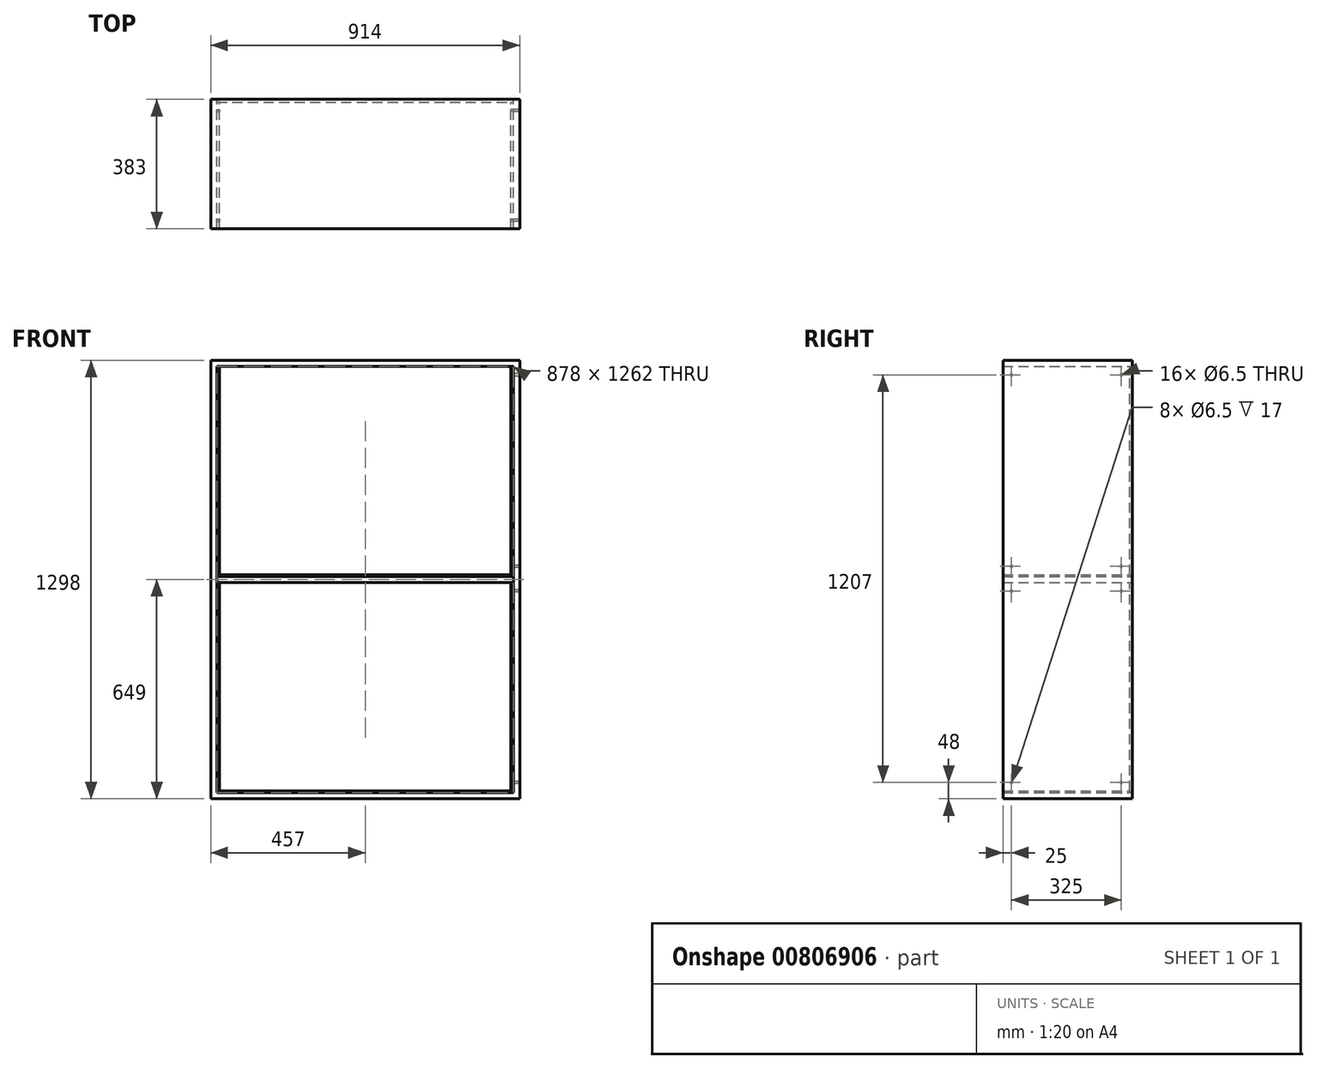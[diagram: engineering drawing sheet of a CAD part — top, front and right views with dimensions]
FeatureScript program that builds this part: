
annotation { "Feature Type Name" : "Feature", "Feature Type Description" : "" }
export const myFeature = defineFeature(function(context is Context, id is Id, definition is map)
    precondition{}
    {
        {
            var Q0;
            Q0=qCreatedBy(makeId("Front.planeOp"),FACE);
            var sketch = newSketch(context, id + "F0", { "sketchPlane" : qUnion([Q0])});
            skLineSegment(sketch, "E0.bottom", {"start": v(457, -649) * mm, "end": v(-457, -649) * mm});
            skLineSegment(sketch, "E0.top", {"start": v(457, 649) * mm, "end": v(-457, 649) * mm});
            skLineSegment(sketch, "E0.left", {"start": v(457, -649) * mm, "end": v(457, 649) * mm});
            skLineSegment(sketch, "E0.right", {"start": v(-457, -649) * mm, "end": v(-457, 649) * mm});
            skPoint(sketch, "E0.middle", {"position": v(0, 0) * mm});
            skLineSegment(sketch, "E1.bottom", {"start": v(439, 631) * mm, "end": v(-439, 631) * mm});
            skLineSegment(sketch, "E1.top", {"start": v(439, -631) * mm, "end": v(-439, -631) * mm});
            skLineSegment(sketch, "E1.left", {"start": v(439, 631) * mm, "end": v(439, -631) * mm});
            skLineSegment(sketch, "E1.right", {"start": v(-439, 631) * mm, "end": v(-439, -631) * mm});
            skLineSegment(sketch, "E2", {"start": v(-439, 0) * mm, "end": v(-457, 0) * mm, "construction": true});
            skLineSegment(sketch, "E3", {"start": v(439, 0) * mm, "end": v(457, 0) * mm, "construction": true});
            skLineSegment(sketch, "E4", {"start": v(0, 631) * mm, "end": v(0, 649) * mm, "construction": true});
            skLineSegment(sketch, "E5", {"start": v(0, -631) * mm, "end": v(0, -649) * mm, "construction": true});
            skSolve(sketch);
        }
        {
            var Q0;
            Q0 = qSketchRegion(id + "F0", true);
            extrude(context, id + "F1", {"entities" : qUnion([Q0]), "depth" : (375 + 8) * mm, "offsetDistance" : 25 * mm});
        }
        {
            var Q0;
            Q0=makeQuery(id+"F1.opExtrude","SWEPT_FACE",FACE,{"disambiguationData":[OSD([sQuery(id+"F0.wireOp",EDGE,"E1.right")])]});
            var sketch = newSketch(context, id + "F2", { "sketchPlane" : qUnion([Q0])});
            skLineSegment(sketch, "E6.bottom", {"start": v(-383, 9) * mm, "end": v(0, 9) * mm});
            skLineSegment(sketch, "E6.top", {"start": v(-383, -9) * mm, "end": v(0, -9) * mm});
            skLineSegment(sketch, "E6.left", {"start": v(-383, 9) * mm, "end": v(-383, -9) * mm});
            skLineSegment(sketch, "E6.right", {"start": v(0, 9) * mm, "end": v(0, -9) * mm});
            skSolve(sketch);
        }
        {
            var Q0;
            Q0 = qSketchRegion(id + "F2", true);
            var Q1;
            Q1=makeQuery(id+"F1.opExtrude","SWEPT_FACE",FACE,{"disambiguationData":[OSD([sQuery(id+"F0.wireOp",EDGE,"E1.left")])]});
            extrude(context, id + "F3", {"entities" : qUnion([Q0]), "endBound" : BoundingType.UP_TO_SURFACE, "depth" : 25 * mm, "endBoundEntityFace" : qUnion([Q1]), "offsetDistance" : 25 * mm});
        }
        {
            var Q0;
            Q0=makeQuery(id+"F3.opExtrude","SWEPT_FACE",FACE,{"disambiguationData":[OSD([sQuery(id+"F2.wireOp",EDGE,"E6.bottom")])]});
            var sketch = newSketch(context, id + "F4", { "sketchPlane" : qUnion([Q0])});
            skLineSegment(sketch, "E7.bottom", {"start": v(-439, -383) * mm, "end": v(439, -383) * mm});
            skLineSegment(sketch, "E7.top", {"start": v(-439, -8) * mm, "end": v(439, -8) * mm});
            skLineSegment(sketch, "E7.left", {"start": v(-439, -383) * mm, "end": v(-439, -8) * mm});
            skLineSegment(sketch, "E7.right", {"start": v(439, -383) * mm, "end": v(439, -8) * mm});
            skSolve(sketch);
        }
        {
            var Q0;
            Q0 = qSketchRegion(id + "F4", true);
            extrude(context, id + "F5", {"entities" : qUnion([Q0]), "depth" : 5 * mm, "offsetDistance" : 25 * mm});
        }
        {
            var Q0;
            Q0=makeQuery(id+"F1.opExtrude","SWEPT_FACE",FACE,{"disambiguationData":[OSD([sQuery(id+"F0.wireOp",EDGE,"E1.left")])]});
            var sketch = newSketch(context, id + "F6", { "sketchPlane" : qUnion([Q0])});
            skLineSegment(sketch, "E8.bottom", {"start": v(383, 14) * mm, "end": v(8, 14) * mm});
            skLineSegment(sketch, "E8.top", {"start": v(383, 631) * mm, "end": v(8, 631) * mm});
            skLineSegment(sketch, "E8.left", {"start": v(383, 14) * mm, "end": v(383, 631) * mm});
            skLineSegment(sketch, "E8.right", {"start": v(8, 14) * mm, "end": v(8, 631) * mm});
            skSolve(sketch);
        }
        {
            var Q0;
            Q0 = qSketchRegion(id + "F6", true);
            extrude(context, id + "F7", {"entities" : qUnion([Q0]), "depth" : 8 * mm, "offsetDistance" : 25 * mm});
        }
        {
            var Q0;
            Q0=makeQuery(id+"F7.opExtrude","CAP_FACE",FACE,{"disambiguationData":[OSD([sQuery(id+"F6.wireOp",EDGE,"E8.bottom"),sQuery(id+"F6.wireOp",EDGE,"E8.top"),sQuery(id+"F6.wireOp",EDGE,"E8.left"),sQuery(id+"F6.wireOp",EDGE,"E8.right")])],"isStart":false});
            var sketch = newSketch(context, id + "F8", { "sketchPlane" : qUnion([Q0])});
            skCircle(sketch, "E9", {"center": v(358, 39) * mm, "radius": 3.25 * mm});
            skLineSegment(sketch, "E10", {"start": v(358, 39) * mm, "end": v(383, 39) * mm, "construction": true});
            skLineSegment(sketch, "E11", {"start": v(358, 39) * mm, "end": v(358, 14) * mm, "construction": true});
            skCircle(sketch, "E12.0.1.0", {"center": v(358, 606) * mm, "radius": 3.25 * mm});
            skCircle(sketch, "E12.1.0.0", {"center": v(33, 39) * mm, "radius": 3.25 * mm});
            skCircle(sketch, "E12.1.1.0", {"center": v(33, 606) * mm, "radius": 3.25 * mm});
            skLineSegment(sketch, "E12.direction1", {"start": v(358, 39) * mm, "end": v(33, 39) * mm, "construction": true});
            skLineSegment(sketch, "E12.direction2", {"start": v(358, 39) * mm, "end": v(358, 606) * mm, "construction": true});
            skSolve(sketch);
        }
        {
            var Q0;
            Q0 = qSketchRegion(id + "F8", true);
            extrude(context, id + "F9", {"entities" : qUnion([Q0]), "operationType" : NewBodyOperationType.REMOVE, "oppositeDirection" : true, "depth" : 25 * mm, "offsetDistance" : 25 * mm});
        }
        {
            var Q0;
            Q0=makeQuery(id+"F7.opExtrude","SWEPT_BODY",BODY,{"disambiguationData":[OSD([sQuery(id+"F6.wireOp",EDGE,"E8.bottom"),sQuery(id+"F6.wireOp",EDGE,"E8.top"),sQuery(id+"F6.wireOp",EDGE,"E8.left"),sQuery(id+"F6.wireOp",EDGE,"E8.right")])]});
            var Q1;
            Q1=qCreatedBy(makeId("Right.planeOp"),FACE);
            mirror(context, id + "F10", {"entities" : qUnion([Q0]), "mirrorPlane" : qUnion([Q1])});
        }
        {
            var Q0;
            Q0=makeQuery(id+"F5.opExtrude","SWEPT_BODY",BODY,{"disambiguationData":[OSD([sQuery(id+"F4.wireOp",EDGE,"E7.bottom"),sQuery(id+"F4.wireOp",EDGE,"E7.top"),sQuery(id+"F4.wireOp",EDGE,"E7.left"),sQuery(id+"F4.wireOp",EDGE,"E7.right")])]});
            transform(context, id + "F11", {"entities" : qUnion([Q0]), "transformType" : TransformType.TRANSLATION_3D, "dx" : 0 * mm, "dy" : 0 * mm, "dz" : -640 * mm, "makeCopy" : true});
        }
        {
            var Q0;
            Q0=makeQuery(id+"F1.opExtrude","SWEPT_FACE",FACE,{"disambiguationData":[OSD([sQuery(id+"F0.wireOp",EDGE,"E1.left")])]});
            var sketch = newSketch(context, id + "F12", { "sketchPlane" : qUnion([Q0])});
            skLineSegment(sketch, "E13.bottom", {"start": v(383, -626) * mm, "end": v(8, -626) * mm});
            skLineSegment(sketch, "E13.top", {"start": v(383, -9) * mm, "end": v(8, -9) * mm});
            skLineSegment(sketch, "E13.left", {"start": v(383, -626) * mm, "end": v(383, -9) * mm});
            skLineSegment(sketch, "E13.right", {"start": v(8, -626) * mm, "end": v(8, -9) * mm});
            skSolve(sketch);
        }
        {
            var Q0;
            Q0 = qSketchRegion(id + "F12", true);
            extrude(context, id + "F13", {"entities" : qUnion([Q0]), "depth" : 8 * mm, "offsetDistance" : 25 * mm});
        }
        {
            var Q0;
            Q0=makeQuery(id+"F13.opExtrude","CAP_FACE",FACE,{"disambiguationData":[OSD([sQuery(id+"F12.wireOp",EDGE,"E13.bottom"),sQuery(id+"F12.wireOp",EDGE,"E13.top"),sQuery(id+"F12.wireOp",EDGE,"E13.left"),sQuery(id+"F12.wireOp",EDGE,"E13.right")])],"isStart":false});
            var sketch = newSketch(context, id + "F14", { "sketchPlane" : qUnion([Q0])});
            skCircle(sketch, "E14", {"center": v(358, -601) * mm, "radius": 3.25 * mm});
            skLineSegment(sketch, "E15", {"start": v(358, -601) * mm, "end": v(383, -601) * mm, "construction": true});
            skLineSegment(sketch, "E16", {"start": v(358, -601) * mm, "end": v(358, -626) * mm, "construction": true});
            skCircle(sketch, "E17.0.1.0", {"center": v(358, -34) * mm, "radius": 3.25 * mm});
            skCircle(sketch, "E17.1.0.0", {"center": v(33, -601) * mm, "radius": 3.25 * mm});
            skCircle(sketch, "E17.1.1.0", {"center": v(33, -34) * mm, "radius": 3.25 * mm});
            skLineSegment(sketch, "E17.direction1", {"start": v(358, -601) * mm, "end": v(33, -601) * mm, "construction": true});
            skLineSegment(sketch, "E17.direction2", {"start": v(358, -601) * mm, "end": v(358, -34) * mm, "construction": true});
            skSolve(sketch);
        }
        {
            var Q0;
            Q0 = qSketchRegion(id + "F14", true);
            extrude(context, id + "F15", {"entities" : qUnion([Q0]), "operationType" : NewBodyOperationType.REMOVE, "oppositeDirection" : true, "depth" : 25 * mm, "offsetDistance" : 25 * mm});
        }
        {
            var Q0;
            Q0=makeQuery(id+"F13.opExtrude","SWEPT_BODY",BODY,{"disambiguationData":[OSD([sQuery(id+"F12.wireOp",EDGE,"E13.bottom"),sQuery(id+"F12.wireOp",EDGE,"E13.top"),sQuery(id+"F12.wireOp",EDGE,"E13.left"),sQuery(id+"F12.wireOp",EDGE,"E13.right")])]});
            var Q1;
            Q1=qCreatedBy(makeId("Right.planeOp"),FACE);
            mirror(context, id + "F16", {"entities" : qUnion([Q0]), "mirrorPlane" : qUnion([Q1])});
        }
    });
